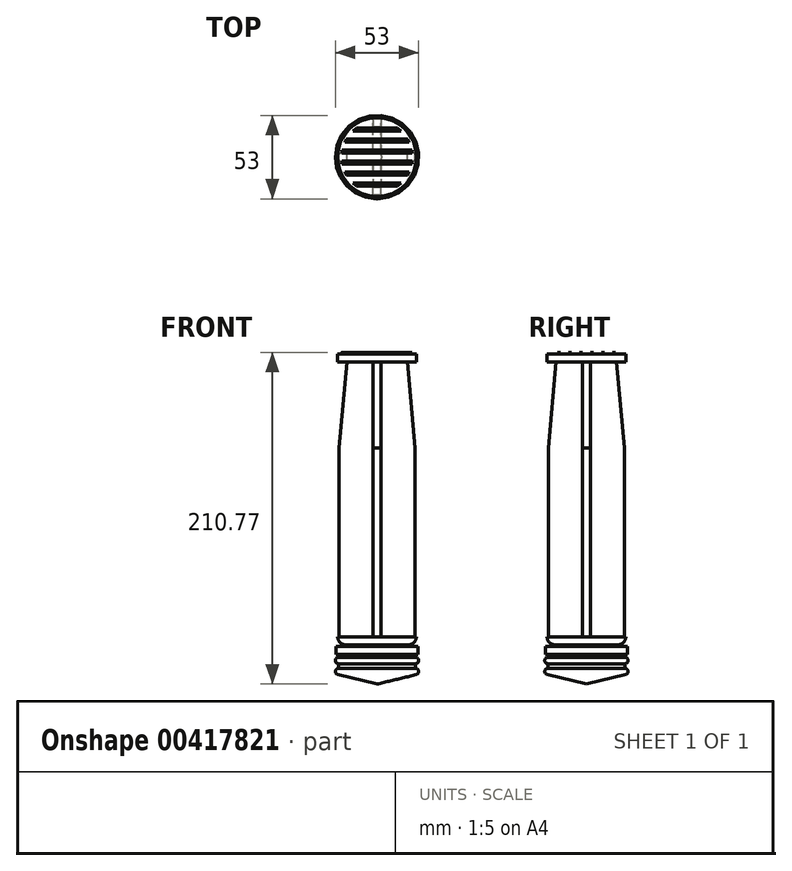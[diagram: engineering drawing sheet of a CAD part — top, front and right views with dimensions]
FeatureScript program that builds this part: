
annotation { "Feature Type Name" : "Feature", "Feature Type Description" : "" }
export const myFeature = defineFeature(function(context is Context, id is Id, definition is map)
    precondition{}
    {
        {
            var Q0;
            Q0=qCreatedBy(makeId("Top.planeOp"),FACE);
            var sketch = newSketch(context, id + "F0", { "sketchPlane" : qUnion([Q0])});
            skCircle(sketch, "E0", {"center": v(0, 0) * mm, "radius": 25 * mm});
            skSolve(sketch);
        }
        {
            var Q0;
            Q0=makeQuery(id+"F0.imprint","IMPRINT",FACE,{"disambiguationData":[TD([[makeQuery(id+"F0.imprint","IMPRINT",EDGE,{"derivedFrom":sQuery(id+"F0.wireOp",EDGE,"E0")}),1.0]])]});
            extrude(context, id + "F1", {"entities" : qUnion([Q0]), "depth" : 5 * mm});
        }
        {
            var Q0;
            Q0=qCreatedBy(makeId("Front.planeOp"),FACE);
            var sketch = newSketch(context, id + "F2", { "sketchPlane" : qUnion([Q0])});
            skLineSegment(sketch, "E1.0", {"start": v(-25, 5) * mm, "end": v(25, 5) * mm});
            skPoint(sketch, "E2", {"position": v(-24, 5) * mm});
            skPoint(sketch, "E3", {"position": v(24, 5) * mm});
            skLineSegment(sketch, "E4", {"start": v(-24, 5) * mm, "end": v(-24, 125) * mm});
            skLineSegment(sketch, "E5", {"start": v(-24, 125) * mm, "end": v(-18.77, 184.77) * mm});
            skLineSegment(sketch, "E6.MirrorCS", {"start": v(24, 5) * mm, "end": v(24, 125) * mm});
            skLineSegment(sketch, "E7.MirrorCS", {"start": v(24, 125) * mm, "end": v(18.77, 184.77) * mm});
            skLineSegment(sketch, "E8", {"start": v(-18.77, 184.77) * mm, "end": v(18.77, 184.77) * mm});
            skSolve(sketch);
        }
        {
            var Q0;
            {var subQ1=sQuery(id+"F2.wireOp",EDGE,"E4");Q0=makeQuery(id+"F2.imprint","IMPRINT",FACE,{"disambiguationData":[TD([[makeQuery(id+"F2.imprint","IMPRINT",EDGE,{"derivedFrom":subQ1}),-1.0]])]});}
            extrude(context, id + "F3", {"entities" : qUnion([Q0]), "operationType" : NewBodyOperationType.ADD, "endBound" : BoundingType.SYMMETRIC, "depth" : 5 * mm});
        }
        {
            var Q0;
            Q0=qCreatedBy(makeId("Right.planeOp"),FACE);
            var sketch = newSketch(context, id + "F4", { "sketchPlane" : qUnion([Q0])});
            skLineSegment(sketch, "E9.0", {"start": v(-25, 5) * mm, "end": v(25, 5) * mm});
            skPoint(sketch, "E10", {"position": v(-24, 5) * mm});
            skPoint(sketch, "E11", {"position": v(24, 5) * mm});
            skLineSegment(sketch, "E12", {"start": v(-24, 5) * mm, "end": v(-24, 125) * mm});
            skLineSegment(sketch, "E13", {"start": v(-24, 125) * mm, "end": v(-18.77, 184.77) * mm});
            skLineSegment(sketch, "E14.MirrorCS", {"start": v(24, 5) * mm, "end": v(24, 125) * mm});
            skLineSegment(sketch, "E15.MirrorCS", {"start": v(24, 125) * mm, "end": v(18.77, 184.77) * mm});
            skLineSegment(sketch, "E16", {"start": v(-18.77, 184.77) * mm, "end": v(18.77, 184.77) * mm});
            skSolve(sketch);
        }
        {
            var Q0;
            {var subQ1=sQuery(id+"F4.wireOp",EDGE,"E12");Q0=makeQuery(id+"F4.imprint","IMPRINT",FACE,{"disambiguationData":[TD([[makeQuery(id+"F4.imprint","IMPRINT",EDGE,{"derivedFrom":subQ1}),-1.0]])]});}
            extrude(context, id + "F5", {"entities" : qUnion([Q0]), "operationType" : NewBodyOperationType.ADD, "endBound" : BoundingType.SYMMETRIC, "depth" : 5 * mm});
        }
        {
            var Q0;
            Q0=makeQuery(id+"F5.boolean.opBoolean","MERGE",FACE,{"derivedFrom":[makeQuery(id+"F3.opExtrude","SWEPT_FACE",FACE,{"disambiguationData":[OSD([sQuery(id+"F2.wireOp",EDGE,"E8")])]}),makeQuery(id+"F5.opExtrude","SWEPT_FACE",FACE,{"disambiguationData":[OSD([sQuery(id+"F4.wireOp",EDGE,"E16")])]})]});
            var sketch = newSketch(context, id + "F6", { "sketchPlane" : qUnion([Q0])});
            skCircle(sketch, "E17.0", {"center": v(0, 0) * mm, "radius": 25 * mm});
            skSolve(sketch);
        }
        {
            var Q0;
            Q0=makeQuery(id+"F6.imprint","IMPRINT",FACE,{"disambiguationData":[TD([[makeQuery(id+"F6.imprint","IMPRINT",EDGE,{"derivedFrom":sQuery(id+"F6.wireOp",EDGE,"E17.0")}),1.0]])]});
            extrude(context, id + "F7", {"entities" : qUnion([Q0]), "operationType" : NewBodyOperationType.ADD, "oppositeDirection" : true, "depth" : 5 * mm});
        }
        {
            var Q0;
            Q0=qCreatedBy(makeId("Right.planeOp"),FACE);
            var sketch = newSketch(context, id + "F8", { "sketchPlane" : qUnion([Q0])});
            skLineSegment(sketch, "E18", {"start": v(0, 0) * mm, "end": v(-3.04, 0) * mm});
            skLineSegment(sketch, "E19", {"start": v(-3.04, 0) * mm, "end": v(-3.04, -1) * mm});
            skLineSegment(sketch, "E20", {"start": v(-3.04, -1) * mm, "end": v(-26, -1) * mm});
            skLineSegment(sketch, "E21", {"start": v(-26, -1) * mm, "end": v(-26, -6) * mm});
            skLineSegment(sketch, "E22", {"start": v(-26, -6) * mm, "end": v(-24.5, -6) * mm});
            skLineSegment(sketch, "E23", {"start": v(-24.5, -6) * mm, "end": v(-24.5, -8) * mm});
            skArc(sketch, "E24", {"start": v(-24.5, -8) * mm, "mid": v(-26.5, -10) * mm, "end": v(-24.5, -12) * mm});
            skLineSegment(sketch, "E25", {"start": v(-24.5, -12) * mm, "end": v(-24.5, -15) * mm});
            skArc(sketch, "E26", {"start": v(-24.5, -15) * mm, "mid": v(-26.5, -17) * mm, "end": v(-24.5, -19) * mm});
            skLineSegment(sketch, "E27", {"start": v(0, -25) * mm, "end": v(0, 0) * mm});
            skLineSegment(sketch, "E28.0", {"start": v(-3.04, 0) * mm, "end": v(25, 0) * mm});
            skPoint(sketch, "E29.orphan", {"position": v(-25, 0) * mm});
            skLineSegment(sketch, "E30", {"start": v(-24.23, -8) * mm, "end": v(-24.5, -8) * mm});
            skLineSegment(sketch, "E31", {"start": v(0, -25) * mm, "end": v(-24.97, -18.94) * mm});
            skSolve(sketch);
        }
        {
            var Q0;
            {var subQ1=sQuery(id+"F8.wireOp",EDGE,"E19");Q0=makeQuery(id+"F8.imprint","IMPRINT",FACE,{"disambiguationData":[TD([[makeQuery(id+"F8.imprint","IMPRINT",EDGE,{"derivedFrom":subQ1}),1.0]])]});}
            var Q1;
            Q1=sQuery(id+"F8.wireOp",EDGE,"E27");
            revolve(context, id + "F9", {"entities" : qUnion([Q0]), "axis" : qUnion([Q1]), "revolveType" : RevolveType.FULL});
        }
        {
            var Q0;
            Q0=makeQuery(id+"F1.opExtrude","CAP_EDGE",EDGE,{"disambiguationData":[OSD([sQuery(id+"F0.wireOp",EDGE,"E0")])],"isStart":true});
            fillet(context, id + "F10", {"entities" : qUnion([Q0]), "radius" : 5 * mm, "tangentPropagation" : true, "allowEdgeOverflow" : false});
        }
        {
            var Q0;
            {var subQ0=sQuery(id+"F4.wireOp",EDGE,"E16");var subQ1=sQuery(id+"F2.wireOp",EDGE,"E8");Q0=makeQuery(id+"F7.boolean.opBoolean","MERGE",FACE,{"derivedFrom":[makeQuery(id+"F5.boolean.opBoolean","MERGE",FACE,{"derivedFrom":[makeQuery(id+"F3.opExtrude","SWEPT_FACE",FACE,{"disambiguationData":[OSD([subQ1])]}),makeQuery(id+"F5.opExtrude","SWEPT_FACE",FACE,{"disambiguationData":[OSD([subQ0])]})]}),makeQuery(id+"F7.opExtrude","CAP_FACE",FACE,{"disambiguationData":[OSD([sQuery(id+"F2.wireOp",EDGE,"E5"),sQuery(id+"F2.wireOp",EDGE,"E7.MirrorCS"),subQ1,sQuery(id+"F4.wireOp",EDGE,"E13"),sQuery(id+"F4.wireOp",EDGE,"E15.MirrorCS"),subQ0,sQuery(id+"F6.wireOp",EDGE,"E17.0")])],"isStart":true})]});}
            var sketch = newSketch(context, id + "F11", { "sketchPlane" : qUnion([Q0])});
            skCircle(sketch, "E32", {"center": v(0, 0) * mm, "radius": 22.5 * mm});
            skLineSegment(sketch, "E33", {"start": v(-12.8, -18.5) * mm, "end": v(12.8, -18.5) * mm});
            skLineSegment(sketch, "E34", {"start": v(-15.3, -16.5) * mm, "end": v(15.3, -16.5) * mm});
            skLineSegment(sketch, "E35", {"start": v(-19.34, -11.5) * mm, "end": v(19.34, -11.5) * mm});
            skLineSegment(sketch, "E36", {"start": v(-20.4, -9.5) * mm, "end": v(20.4, -9.5) * mm});
            skLineSegment(sketch, "E37", {"start": v(-22.05, -4.5) * mm, "end": v(22.05, -4.5) * mm});
            skLineSegment(sketch, "E38", {"start": v(-22.36, -2.5) * mm, "end": v(22.36, -2.5) * mm});
            skLineSegment(sketch, "E39.MirrorCS", {"start": v(-22.36, 2.5) * mm, "end": v(22.36, 2.5) * mm});
            skLineSegment(sketch, "E40.MirrorCS", {"start": v(-22.05, 4.5) * mm, "end": v(22.05, 4.5) * mm});
            skLineSegment(sketch, "E41.MirrorCS", {"start": v(-20.4, 9.5) * mm, "end": v(20.4, 9.5) * mm});
            skLineSegment(sketch, "E42.MirrorCS", {"start": v(-19.34, 11.5) * mm, "end": v(19.34, 11.5) * mm});
            skLineSegment(sketch, "E43.MirrorCS", {"start": v(-12.8, 18.5) * mm, "end": v(12.8, 18.5) * mm});
            skLineSegment(sketch, "E44.MirrorCS", {"start": v(-15.3, 16.5) * mm, "end": v(15.3, 16.5) * mm});
            skSolve(sketch);
        }
        {
            var Q0;
            {var subQ0=sQuery(id+"F11.wireOp",EDGE,"E33");Q0=makeQuery(id+"F11.imprint","IMPRINT",FACE,{"disambiguationData":[TD([[makeQuery(id+"F11.imprint","IMPRINT",EDGE,{"derivedFrom":subQ0}),1.0]])]});}
            var Q1;
            {var subQ0=sQuery(id+"F11.wireOp",EDGE,"E35");Q1=makeQuery(id+"F11.imprint","IMPRINT",FACE,{"disambiguationData":[TD([[makeQuery(id+"F11.imprint","IMPRINT",EDGE,{"derivedFrom":subQ0}),1.0]])]});}
            var Q2;
            {var subQ0=sQuery(id+"F11.wireOp",EDGE,"E37");Q2=makeQuery(id+"F11.imprint","IMPRINT",FACE,{"disambiguationData":[TD([[makeQuery(id+"F11.imprint","IMPRINT",EDGE,{"derivedFrom":subQ0}),1.0]])]});}
            var Q3;
            {var subQ0=sQuery(id+"F11.wireOp",EDGE,"E39.MirrorCS");Q3=makeQuery(id+"F11.imprint","IMPRINT",FACE,{"disambiguationData":[TD([[makeQuery(id+"F11.imprint","IMPRINT",EDGE,{"derivedFrom":subQ0}),1.0]])]});}
            var Q4;
            {var subQ0=sQuery(id+"F11.wireOp",EDGE,"E41.MirrorCS");Q4=makeQuery(id+"F11.imprint","IMPRINT",FACE,{"disambiguationData":[TD([[makeQuery(id+"F11.imprint","IMPRINT",EDGE,{"derivedFrom":subQ0}),1.0]])]});}
            var Q5;
            {var subQ0=sQuery(id+"F11.wireOp",EDGE,"E43.MirrorCS");Q5=makeQuery(id+"F11.imprint","IMPRINT",FACE,{"disambiguationData":[TD([[makeQuery(id+"F11.imprint","IMPRINT",EDGE,{"derivedFrom":subQ0}),-1.0]])]});}
            extrude(context, id + "F12", {"entities" : qUnion([Q0, Q1, Q2, Q3, Q4, Q5]), "operationType" : NewBodyOperationType.ADD, "depth" : 1 * mm});
        }
    });
